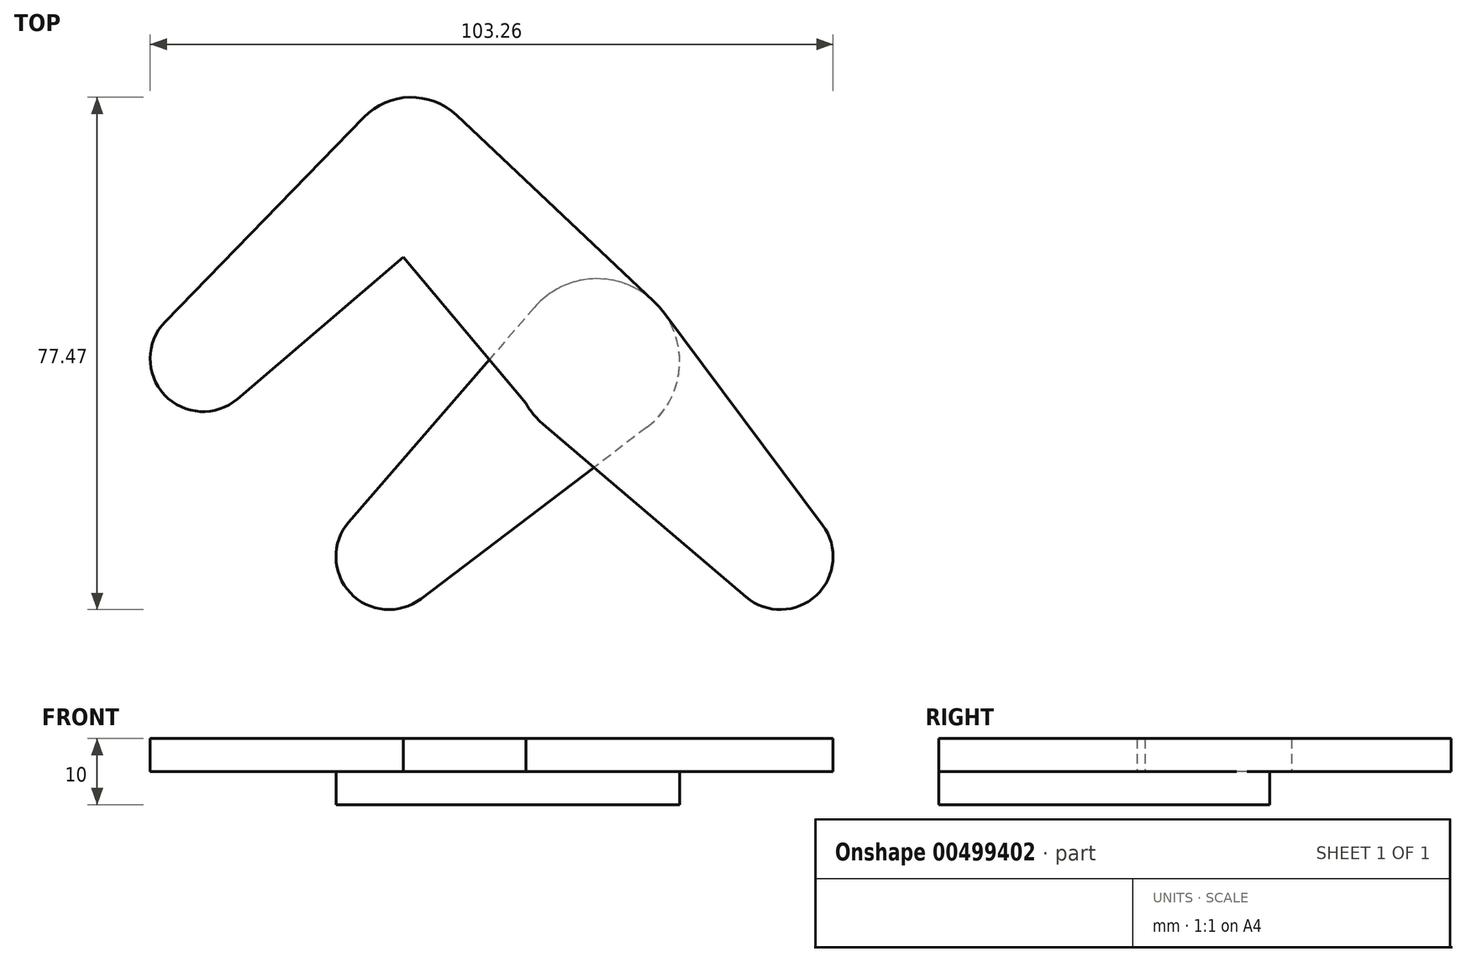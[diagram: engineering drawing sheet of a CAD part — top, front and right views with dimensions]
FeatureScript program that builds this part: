
annotation { "Feature Type Name" : "Feature", "Feature Type Description" : "" }
export const myFeature = defineFeature(function(context is Context, id is Id, definition is map)
    precondition{}
    {
        {
            var Q0;
            Q0=qCreatedBy(makeId("Top.planeOp"),FACE);
            var sketch = newSketch(context, id + "F0", { "sketchPlane" : qUnion([Q0])});
            skCircle(sketch, "E0", {"center": v(-47.47, 29.94) * mm, "radius": 8 * mm});
            skCircle(sketch, "E1", {"center": v(-16, 59.47) * mm, "radius": 10 * mm});
            skCircle(sketch, "E2", {"center": v(12.1, 29.52) * mm, "radius": 12.5 * mm});
            skCircle(sketch, "E3", {"center": v(39.8, 0) * mm, "radius": 8 * mm});
            skLineSegment(sketch, "E4", {"start": v(-16, 59.47) * mm, "end": v(39.8, 0) * mm, "construction": true});
            skLineSegment(sketch, "E5", {"start": v(-16, 59.47) * mm, "end": v(-62.96, 15.4) * mm, "construction": true});
            skLineSegment(sketch, "E6", {"start": v(12.1, 29.52) * mm, "end": v(-31.58, -11.44) * mm, "construction": true});
            skCircle(sketch, "E7", {"center": v(-19.38, 0) * mm, "radius": 8 * mm});
            skLineSegment(sketch, "E8", {"start": v(-47.47, 29.94) * mm, "end": v(-19.38, 0) * mm, "construction": true});
            skLineSegment(sketch, "E9", {"start": v(-53.2, 35.52) * mm, "end": v(-23.17, 66.43) * mm});
            skLineSegment(sketch, "E10", {"start": v(-42.27, 23.86) * mm, "end": v(-9.5, 51.86) * mm});
            skLineSegment(sketch, "E11", {"start": v(-23.66, 53.05) * mm, "end": v(1.32, 23.18) * mm});
            skLineSegment(sketch, "E12", {"start": v(-9.13, 66.74) * mm, "end": v(20.67, 38.62) * mm});
            skLineSegment(sketch, "E13", {"start": v(22.1, 37.01) * mm, "end": v(46.2, 4.8) * mm});
            skLineSegment(sketch, "E14", {"start": v(3.98, 20.01) * mm, "end": v(34.6, -6.09) * mm});
            skLineSegment(sketch, "E15", {"start": v(19.65, 19.57) * mm, "end": v(-14.54, -6.37) * mm});
            skLineSegment(sketch, "E16", {"start": v(2.64, 37.7) * mm, "end": v(-25.43, 5.23) * mm});
            skSolve(sketch);
        }
        {
            var Q0;
            {var subQ0=sQuery(id+"F0.wireOp",EDGE,"E10");var subQ1=sQuery(id+"F0.wireOp",EDGE,"E1");var subQ2=makeQuery(id+"F0.imprint","INTERSECT",VERTEX,{"derivedFrom":[subQ1,subQ0]});Q0=makeQuery(id+"F0.imprint","IMPRINT",FACE,{"disambiguationData":[TD([[makeQuery(id+"F0.imprint","IMPRINT",EDGE,{"disambiguationData":[TD([[subQ2,1.0]])],"derivedFrom":subQ1}),-1.0]])]});}
            var Q1;
            {var subQ5=sQuery(id+"F0.wireOp",EDGE,"E9");Q1=makeQuery(id+"F0.imprint","IMPRINT",FACE,{"disambiguationData":[TD([[makeQuery(id+"F0.imprint","IMPRINT",EDGE,{"derivedFrom":subQ5}),-1.0]])]});}
            var Q2;
            {var subQ0=sQuery(id+"F0.wireOp",EDGE,"E0");var subQ1=makeQuery(id+"F0.imprint","INTERSECT",VERTEX,{"derivedFrom":[subQ0,sQuery(id+"F0.wireOp",EDGE,"E9")]});Q2=makeQuery(id+"F0.imprint","IMPRINT",FACE,{"disambiguationData":[TD([[makeQuery(id+"F0.imprint","IMPRINT",EDGE,{"disambiguationData":[TD([[subQ1,-1.0]])],"derivedFrom":subQ0}),1.0]])]});}
            var Q3;
            {var subQ0=sQuery(id+"F0.wireOp",EDGE,"E1");var subQ1=makeQuery(id+"F0.imprint","INTERSECT",VERTEX,{"derivedFrom":[subQ0,sQuery(id+"F0.wireOp",EDGE,"E9")]});Q3=makeQuery(id+"F0.imprint","IMPRINT",FACE,{"disambiguationData":[TD([[makeQuery(id+"F0.imprint","IMPRINT",EDGE,{"disambiguationData":[TD([[subQ1,1.0]])],"derivedFrom":subQ0}),1.0]])]});}
            var Q4;
            {var subQ5=sQuery(id+"F0.wireOp",EDGE,"E12");Q4=makeQuery(id+"F0.imprint","IMPRINT",FACE,{"disambiguationData":[TD([[makeQuery(id+"F0.imprint","IMPRINT",EDGE,{"derivedFrom":subQ5}),-1.0]])]});}
            var Q5;
            {var subQ0=sQuery(id+"F0.wireOp",EDGE,"E2");var subQ4=makeQuery(id+"F0.imprint","INTERSECT",VERTEX,{"derivedFrom":[subQ0,sQuery(id+"F0.wireOp",EDGE,"E12")]});Q5=makeQuery(id+"F0.imprint","IMPRINT",FACE,{"disambiguationData":[TD([[makeQuery(id+"F0.imprint","IMPRINT",EDGE,{"disambiguationData":[TD([[subQ4,1.0]])],"derivedFrom":subQ0}),1.0]])]});}
            var Q6;
            {var subQ0=sQuery(id+"F0.wireOp",EDGE,"E11");var subQ1=sQuery(id+"F0.wireOp",EDGE,"E2");var subQ2=makeQuery(id+"F0.imprint","INTERSECT",VERTEX,{"derivedFrom":[subQ1,subQ0]});Q6=makeQuery(id+"F0.imprint","IMPRINT",FACE,{"disambiguationData":[TD([[makeQuery(id+"F0.imprint","IMPRINT",EDGE,{"disambiguationData":[TD([[subQ2,1.0]])],"derivedFrom":subQ1}),-1.0]])]});}
            var Q7;
            {var subQ0=sQuery(id+"F0.wireOp",EDGE,"E14");var subQ1=sQuery(id+"F0.wireOp",EDGE,"E2");var subQ2=makeQuery(id+"F0.imprint","INTERSECT",VERTEX,{"derivedFrom":[subQ1,subQ0]});Q7=makeQuery(id+"F0.imprint","IMPRINT",FACE,{"disambiguationData":[TD([[makeQuery(id+"F0.imprint","IMPRINT",EDGE,{"disambiguationData":[TD([[subQ2,-1.0]])],"derivedFrom":subQ1}),-1.0]])]});}
            var Q8;
            {var subQ5=sQuery(id+"F0.wireOp",EDGE,"E13");Q8=makeQuery(id+"F0.imprint","IMPRINT",FACE,{"disambiguationData":[TD([[makeQuery(id+"F0.imprint","IMPRINT",EDGE,{"derivedFrom":subQ5}),-1.0]])]});}
            var Q9;
            {var subQ0=sQuery(id+"F0.wireOp",EDGE,"E3");var subQ1=makeQuery(id+"F0.imprint","INTERSECT",VERTEX,{"derivedFrom":[subQ0,sQuery(id+"F0.wireOp",EDGE,"E13")]});Q9=makeQuery(id+"F0.imprint","IMPRINT",FACE,{"disambiguationData":[TD([[makeQuery(id+"F0.imprint","IMPRINT",EDGE,{"disambiguationData":[TD([[subQ1,-1.0]])],"derivedFrom":subQ0}),1.0]])]});}
            extrude(context, id + "F1", {"entities" : qUnion([Q0, Q1, Q2, Q3, Q4, Q5, Q6, Q7, Q8, Q9]), "depth" : 5 * mm});
        }
        {
            var Q0;
            {var subQ0=sQuery(id+"F0.wireOp",EDGE,"E2");var subQ4=makeQuery(id+"F0.imprint","INTERSECT",VERTEX,{"derivedFrom":[subQ0,sQuery(id+"F0.wireOp",EDGE,"E12")]});Q0=makeQuery(id+"F0.imprint","IMPRINT",FACE,{"disambiguationData":[TD([[makeQuery(id+"F0.imprint","IMPRINT",EDGE,{"disambiguationData":[TD([[subQ4,1.0]])],"derivedFrom":subQ0}),1.0]])]});}
            var Q1;
            {var subQ0=sQuery(id+"F0.wireOp",EDGE,"E11");var subQ1=sQuery(id+"F0.wireOp",EDGE,"E2");var subQ2=makeQuery(id+"F0.imprint","INTERSECT",VERTEX,{"derivedFrom":[subQ1,subQ0]});Q1=makeQuery(id+"F0.imprint","IMPRINT",FACE,{"disambiguationData":[TD([[makeQuery(id+"F0.imprint","IMPRINT",EDGE,{"disambiguationData":[TD([[subQ2,1.0]])],"derivedFrom":subQ1}),-1.0]])]});}
            var Q2;
            {var subQ0=sQuery(id+"F0.wireOp",EDGE,"E14");var subQ1=sQuery(id+"F0.wireOp",EDGE,"E2");var subQ2=makeQuery(id+"F0.imprint","INTERSECT",VERTEX,{"derivedFrom":[subQ1,subQ0]});Q2=makeQuery(id+"F0.imprint","IMPRINT",FACE,{"disambiguationData":[TD([[makeQuery(id+"F0.imprint","IMPRINT",EDGE,{"disambiguationData":[TD([[subQ2,-1.0]])],"derivedFrom":subQ1}),-1.0]])]});}
            var Q3;
            {var subQ0=sQuery(id+"F0.wireOp",EDGE,"E11");var subQ1=sQuery(id+"F0.wireOp",EDGE,"E2");var subQ2=makeQuery(id+"F0.imprint","INTERSECT",VERTEX,{"derivedFrom":[subQ1,subQ0]});Q3=makeQuery(id+"F0.imprint","IMPRINT",FACE,{"disambiguationData":[TD([[makeQuery(id+"F0.imprint","IMPRINT",EDGE,{"disambiguationData":[TD([[subQ2,-1.0]])],"derivedFrom":subQ1}),-1.0]])]});}
            var Q4;
            {var subQ0=sQuery(id+"F0.wireOp",EDGE,"E7");var subQ1=makeQuery(id+"F0.imprint","INTERSECT",VERTEX,{"derivedFrom":[subQ0,sQuery(id+"F0.wireOp",EDGE,"E15")]});Q4=makeQuery(id+"F0.imprint","IMPRINT",FACE,{"disambiguationData":[TD([[makeQuery(id+"F0.imprint","IMPRINT",EDGE,{"disambiguationData":[TD([[subQ1,1.0]])],"derivedFrom":subQ0}),1.0]])]});}
            extrude(context, id + "F2", {"entities" : qUnion([Q0, Q1, Q2, Q3, Q4]), "operationType" : NewBodyOperationType.ADD, "oppositeDirection" : true, "depth" : 5 * mm});
        }
    });
